# Revit family: Wye_Pattern_Strainers-Backflow_Preventor-WATTS-88S
name_source: partatom
category: Pipe Accessories
revit_build: Autodesk Revit 2014 (Build: 20130308_1515(x64)
units: mm (PartAtom-declared; Revit-internal decimal feet)

## types (8) — shared parameters
Assembly Code = F1050
CW Connection = Yes
Country = United States
Description = Stainless Steel, Wye-Pattern Strainers
Finish = Metal-WATTS-Class 600-Stainless Steel
HW Connection = No
Manufacturer = WATTS
Manufacturer Product Line = Strainers
Material = Metal-WATTS-Class 600-Stainless Steel
Max. Working Pressure = 600psi (41.4 bar) at 489°F (254°C) WSP 1440psi (99.3 bar) at 100°F (38°C) WOG
Model = 88S
Price = Prices may vary. Please consult Manufacturer Representative for most up-to-date price list.
Product Documentation Link = http://media.wattswater.com
Product Page URL = http://www.watts.com
Region = North America
URL = http://www.watts.com
Vent Connection = No
Warranty Information = 1 Year Limited Warranty
Waste Connection = No

## per-type parameters (varying)
| type | A | Angle | B | Connection Inlet Description | Connection Outlet Description | Connection Radius | Connection Size | NPT Diameter | NPT Radius | Nominal Depth | Nominal Height | Nominal Radius 2 | Weight | Width |
| 88S - 0.25" | 3" | 15.00° | 2 1/4" | 1/4" NPT Flanged Inlet | 1/4" NPT Flanged Outlet | 1/8" | 1/4" | 1/4" | 1/8" | 3/32" | 1 7/16" | 13/16" | 1.3/0.5 (LB/KG) | 1 1/4" |
| 88S - 0.375" | 3" | 19.00° | 2 1/4" | 3/8" NPT Flanged Inlet | 3/8" NPT Flanged Outlet | 3/16" | 3/8" | 1/4" | 1/8" | 3/32" | 1 7/16" | 13/16" | 1.3/0.5 (LB/KG) | 1 1/4" |
| 88S - 0.5" | 3 13/16" | 20.00° | 2 5/8" | 1/2" NPT Flanged Inlet | 1/2" NPT Flanged Outlet | 1/4" | 1/2" | 1/4" | 1/8" | 3/32" | 1 7/16" | 13/16" | 2.1/0.9 (LB/KG) | 1 1/4" |
| 88S - 0.75" | 4 3/8" | 20.00° | 3 3/16" | 3/4" NPT Flanged Inlet | 3/4" NPT Flanged Outlet | 3/8" | 3/4" | 3/8" | 3/16" | 3/32" | 1 11/16" | 29/32" | 3/1.3 (LB/KG) | 1 1/2" |
| 88S - 1" | 5 3/16" | 23.10° | 3 3/4" | 1" NPT Flanged Inlet | 1" NPT Flanged Outlet | 1/2" | 1" | 1/2" | 1/4" | 3/32" | 1 11/16" | 1 1/16" | 4.5/2 (LB/KG) | 1 3/4" |
| 88S - 1.25" | 5 5/8" | 15.00° | 4 7/8" | 1-1/4" NPT Flanged Inlet | 1-1/4" NPT Flanged Outlet | 5/8" | 1 1/4" | 3/4" | 3/8" | 1/16" | 2 13/32" | 1 9/32" | 5.8/2.6 (LB/KG) | 2" |
| 88S - 1.5" | 6 1/4" | 18.00° | 5" | 1-1/2" NPT Flanged Inlet | 1-1/2" NPT Flanged Outlet | 3/4" | 1 1/2" | 3/4" | 3/8" | 3/32" | 2 17/32" | 1 3/8" | 7/3.1 (LB/KG) | 2 1/2" |
| 88S - 2" | 7 1/2" | 18.00° | 6 1/8" | 2" NPT Flanged Inlet | 2" NPT Flanged Outlet | 1" | 2" | 1" | 1/2" | 3/32" | 2 17/32" | 1 3/8" | 10/4.5 (LB/KG) | 2 1/2" |

## geometry (parser evidence)
native form markers: Sweep x1
no freeform markers — native parametric forms only
